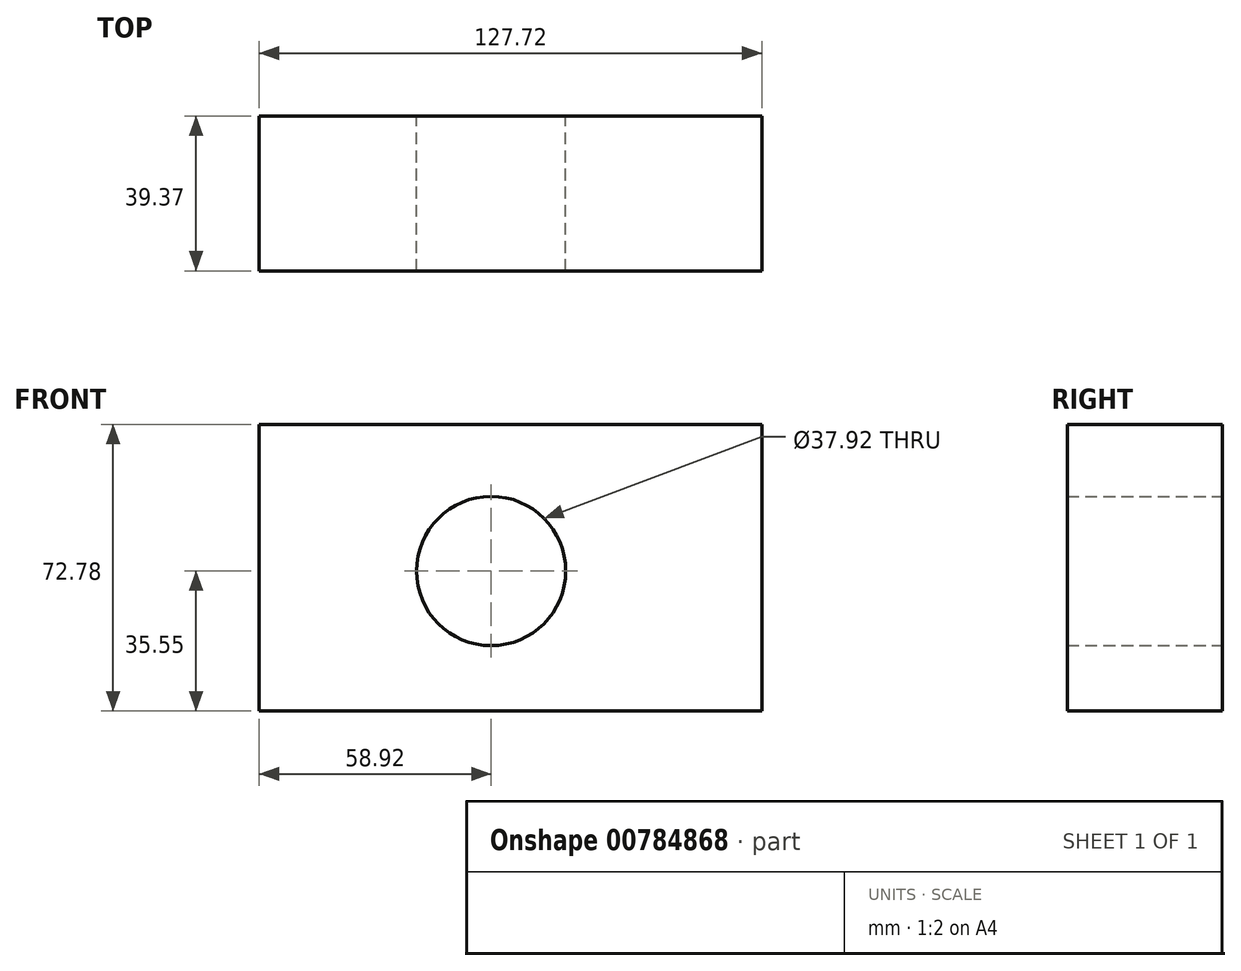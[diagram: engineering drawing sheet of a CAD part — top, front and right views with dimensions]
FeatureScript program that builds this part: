
annotation { "Feature Type Name" : "Feature", "Feature Type Description" : "" }
export const myFeature = defineFeature(function(context is Context, id is Id, definition is map)
    precondition{}
    {
        {
            var Q0;
            Q0=qCreatedBy(makeId("Front.planeOp"),FACE);
            var sketch = newSketch(context, id + "F0", { "sketchPlane" : qUnion([Q0])});
            skLineSegment(sketch, "E0.bottom", {"start": v(-58.92, 37.23) * mm, "end": v(68.8, 37.23) * mm});
            skLineSegment(sketch, "E0.top", {"start": v(-58.92, -35.55) * mm, "end": v(68.8, -35.55) * mm});
            skLineSegment(sketch, "E0.left", {"start": v(-58.92, 37.23) * mm, "end": v(-58.92, -35.55) * mm});
            skLineSegment(sketch, "E0.right", {"start": v(68.8, 37.23) * mm, "end": v(68.8, -35.55) * mm});
            skCircle(sketch, "E1", {"center": v(0, 0) * mm, "radius": 18.96 * mm});
            skCircle(sketch, "E2", {"center": v(0, 0) * mm, "radius": 12.59 * mm});
            skSolve(sketch);
        }
        {
            var Q0;
            Q0=sQuery(id+"F0.wireOp",EDGE,"E1");
            extrude(context, id + "F1", {"bodyType" : ToolBodyType.SURFACE, "surfaceEntities" : qUnion([Q0]), "depth" : 95.25 * mm, "offsetDistance" : 25.4 * mm});
        }
        {
            var Q0;
            Q0 = qSketchRegion(id + "F0", true);
            extrude(context, id + "F2", {"entities" : qUnion([Q0]), "depth" : 39.37 * mm, "offsetDistance" : 25.4 * mm});
        }
    });
